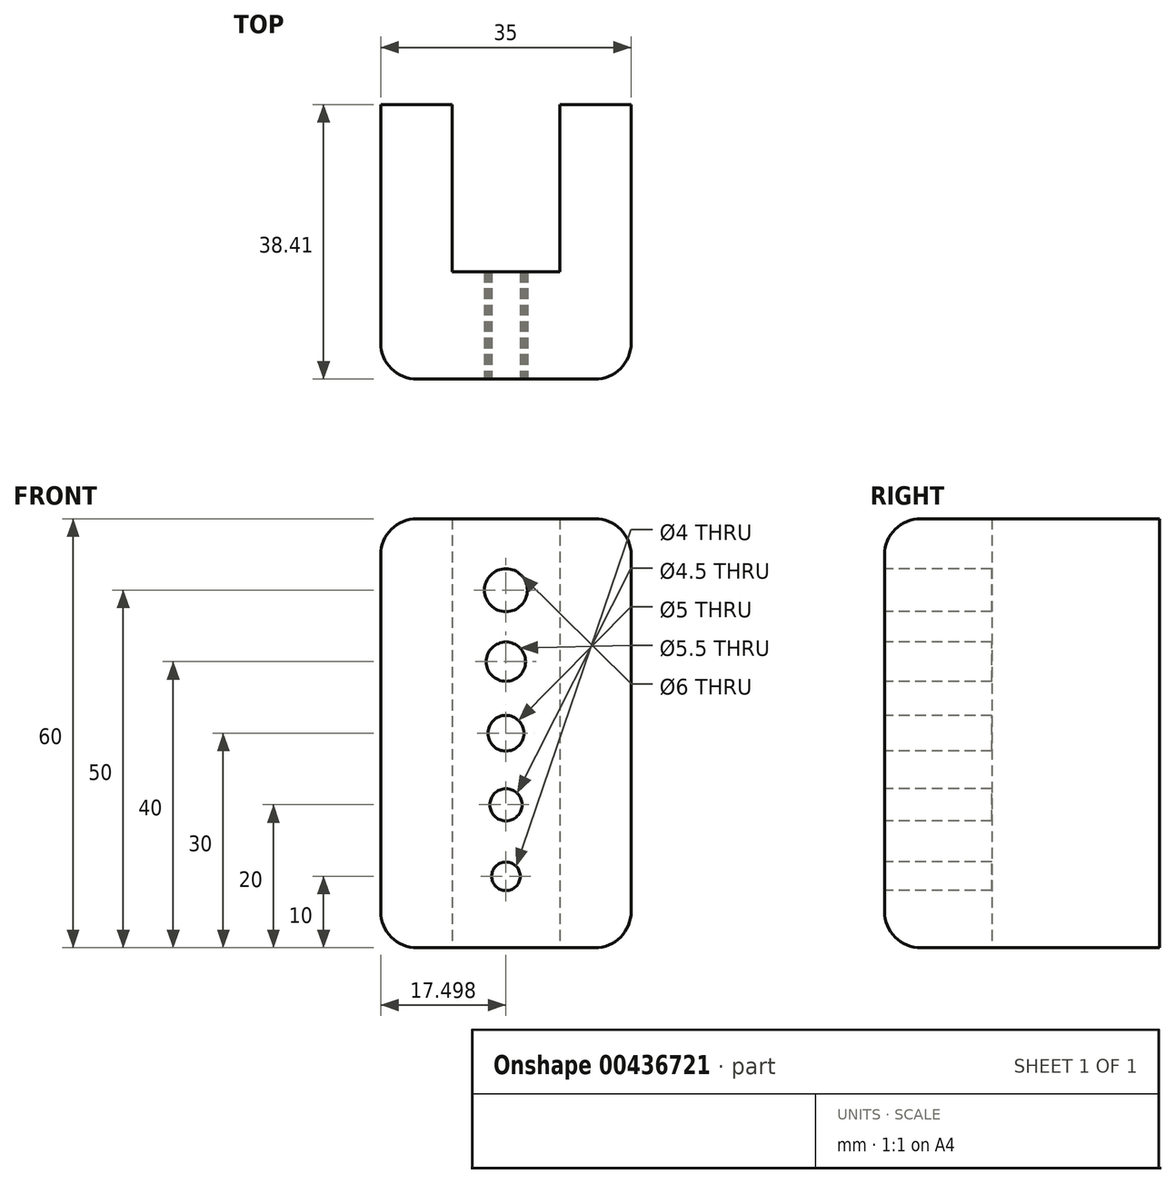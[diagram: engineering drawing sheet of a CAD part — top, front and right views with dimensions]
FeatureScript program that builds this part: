
annotation { "Feature Type Name" : "Feature", "Feature Type Description" : "" }
export const myFeature = defineFeature(function(context is Context, id is Id, definition is map)
    precondition{}
    {
        {
            var Q0;
            Q0=qCreatedBy(makeId("Top.planeOp"),FACE);
            var sketch = newSketch(context, id + "F0", { "sketchPlane" : qUnion([Q0])});
            skLineSegment(sketch, "E0", {"start": v(-17.33, 0) * mm, "end": v(16.64, 0) * mm});
            skLineSegment(sketch, "E1", {"start": v(16.64, 0) * mm, "end": v(16.64, 38.4) * mm});
            skLineSegment(sketch, "E2", {"start": v(16.64, 38.4) * mm, "end": v(6.64, 38.4) * mm});
            skLineSegment(sketch, "E3", {"start": v(6.64, 38.4) * mm, "end": v(6.64, 15) * mm});
            skLineSegment(sketch, "E4", {"start": v(6.64, 15) * mm, "end": v(-8.36, 15) * mm});
            skLineSegment(sketch, "E5", {"start": v(-8.36, 15) * mm, "end": v(-8.36, 38.4) * mm});
            skLineSegment(sketch, "E6", {"start": v(-8.36, 38.4) * mm, "end": v(-18.36, 38.4) * mm});
            skLineSegment(sketch, "E7", {"start": v(-18.36, 38.4) * mm, "end": v(-18.36, 0) * mm});
            skLineSegment(sketch, "E8", {"start": v(-17.33, 0) * mm, "end": v(-18.36, 0) * mm});
            skSolve(sketch);
        }
        {
            var Q0;
            Q0 = qSketchRegion(id + "F0", true);
            extrude(context, id + "F1", {"entities" : qUnion([Q0]), "depth" : 60 * mm});
        }
        {
            var Q0;
            Q0=makeQuery(id+"F1.opExtrude","SWEPT_FACE",FACE,{"disambiguationData":[OSD([sQuery(id+"F0.wireOp",EDGE,"E0"),sQuery(id+"F0.wireOp",EDGE,"E8")])]});
            var sketch = newSketch(context, id + "F2", { "sketchPlane" : qUnion([Q0])});
            skCircle(sketch, "E9", {"center": v(-0.86, 10) * mm, "radius": 2 * mm});
            skCircle(sketch, "E10", {"center": v(-0.86, 30) * mm, "radius": 2.5 * mm});
            skCircle(sketch, "E11", {"center": v(-0.86, 40) * mm, "radius": 2.75 * mm});
            skCircle(sketch, "E12", {"center": v(-0.86, 50) * mm, "radius": 3 * mm});
            skCircle(sketch, "E13", {"center": v(-0.86, 20) * mm, "radius": 2.25 * mm});
            skSolve(sketch);
        }
        {
            var Q0;
            Q0=sQuery(id+"F2.wireOp",VERTEX,"E9.center");
            var Q1;
            Q1=makeQuery(id+"F1.opExtrude","SWEPT_BODY",BODY,{"disambiguationData":[OSD([sQuery(id+"F0.wireOp",EDGE,"E0"),sQuery(id+"F0.wireOp",EDGE,"E1"),sQuery(id+"F0.wireOp",EDGE,"E2"),sQuery(id+"F0.wireOp",EDGE,"E3"),sQuery(id+"F0.wireOp",EDGE,"E4"),sQuery(id+"F0.wireOp",EDGE,"E5"),sQuery(id+"F0.wireOp",EDGE,"E6"),sQuery(id+"F0.wireOp",EDGE,"E7"),sQuery(id+"F0.wireOp",EDGE,"E8")])]});
            hole(context, id + "F3", {"style" : HoleStyle.SIMPLE, "endStyle" : HoleEndStyle.THROUGH, "holeDiameter" : 4 * mm, "isTappedThrough" : true, "tappedDepth" : 12.7 * mm, "tapClearance" : 3, "locations" : qUnion([Q0]), "scope" : qUnion([Q1])});
        }
        {
            var Q0;
            Q0=sQuery(id+"F2.wireOp",VERTEX,"E13.center");
            var Q1;
            Q1=makeQuery(id+"F1.opExtrude","SWEPT_BODY",BODY,{"disambiguationData":[OSD([sQuery(id+"F0.wireOp",EDGE,"E0"),sQuery(id+"F0.wireOp",EDGE,"E1"),sQuery(id+"F0.wireOp",EDGE,"E2"),sQuery(id+"F0.wireOp",EDGE,"E3"),sQuery(id+"F0.wireOp",EDGE,"E4"),sQuery(id+"F0.wireOp",EDGE,"E5"),sQuery(id+"F0.wireOp",EDGE,"E6"),sQuery(id+"F0.wireOp",EDGE,"E7"),sQuery(id+"F0.wireOp",EDGE,"E8")])]});
            hole(context, id + "F4", {"style" : HoleStyle.SIMPLE, "endStyle" : HoleEndStyle.THROUGH, "holeDiameter" : 4.5 * mm, "isTappedThrough" : true, "tappedDepth" : 12.7 * mm, "tapClearance" : 3, "locations" : qUnion([Q0]), "scope" : qUnion([Q1])});
        }
        {
            var Q0;
            Q0=sQuery(id+"F2.wireOp",VERTEX,"E10.center");
            var Q1;
            Q1=makeQuery(id+"F1.opExtrude","SWEPT_BODY",BODY,{"disambiguationData":[OSD([sQuery(id+"F0.wireOp",EDGE,"E0"),sQuery(id+"F0.wireOp",EDGE,"E1"),sQuery(id+"F0.wireOp",EDGE,"E2"),sQuery(id+"F0.wireOp",EDGE,"E3"),sQuery(id+"F0.wireOp",EDGE,"E4"),sQuery(id+"F0.wireOp",EDGE,"E5"),sQuery(id+"F0.wireOp",EDGE,"E6"),sQuery(id+"F0.wireOp",EDGE,"E7"),sQuery(id+"F0.wireOp",EDGE,"E8")])]});
            hole(context, id + "F5", {"style" : HoleStyle.SIMPLE, "endStyle" : HoleEndStyle.THROUGH, "holeDiameter" : 5 * mm, "isTappedThrough" : true, "tappedDepth" : 12.7 * mm, "tapClearance" : 3, "locations" : qUnion([Q0]), "scope" : qUnion([Q1])});
        }
        {
            var Q0;
            Q0=sQuery(id+"F2.wireOp",VERTEX,"E11.center");
            var Q1;
            Q1=makeQuery(id+"F1.opExtrude","SWEPT_BODY",BODY,{"disambiguationData":[OSD([sQuery(id+"F0.wireOp",EDGE,"E0"),sQuery(id+"F0.wireOp",EDGE,"E1"),sQuery(id+"F0.wireOp",EDGE,"E2"),sQuery(id+"F0.wireOp",EDGE,"E3"),sQuery(id+"F0.wireOp",EDGE,"E4"),sQuery(id+"F0.wireOp",EDGE,"E5"),sQuery(id+"F0.wireOp",EDGE,"E6"),sQuery(id+"F0.wireOp",EDGE,"E7"),sQuery(id+"F0.wireOp",EDGE,"E8")])]});
            hole(context, id + "F6", {"style" : HoleStyle.SIMPLE, "endStyle" : HoleEndStyle.THROUGH, "holeDiameter" : 5.5 * mm, "isTappedThrough" : true, "tappedDepth" : 12.7 * mm, "tapClearance" : 3, "locations" : qUnion([Q0]), "scope" : qUnion([Q1])});
        }
        {
            var Q0;
            Q0=sQuery(id+"F2.wireOp",VERTEX,"E12.center");
            var Q1;
            Q1=makeQuery(id+"F1.opExtrude","SWEPT_BODY",BODY,{"disambiguationData":[OSD([sQuery(id+"F0.wireOp",EDGE,"E0"),sQuery(id+"F0.wireOp",EDGE,"E1"),sQuery(id+"F0.wireOp",EDGE,"E2"),sQuery(id+"F0.wireOp",EDGE,"E3"),sQuery(id+"F0.wireOp",EDGE,"E4"),sQuery(id+"F0.wireOp",EDGE,"E5"),sQuery(id+"F0.wireOp",EDGE,"E6"),sQuery(id+"F0.wireOp",EDGE,"E7"),sQuery(id+"F0.wireOp",EDGE,"E8")])]});
            hole(context, id + "F7", {"style" : HoleStyle.SIMPLE, "endStyle" : HoleEndStyle.THROUGH, "holeDiameter" : 6 * mm, "isTappedThrough" : true, "tappedDepth" : 12.7 * mm, "tapClearance" : 3, "locations" : qUnion([Q0]), "scope" : qUnion([Q1])});
        }
        {
            var Q0;
            Q0=makeQuery(id+"F1.opExtrude","SWEPT_EDGE",EDGE,{"disambiguationData":[OSD([sQuery(id+"F0.wireOp",EDGE,"E0"),sQuery(id+"F0.wireOp",EDGE,"E1")])]});
            var Q1;
            Q1=makeQuery(id+"F1.opExtrude","CAP_EDGE",EDGE,{"disambiguationData":[OSD([sQuery(id+"F0.wireOp",EDGE,"E0"),sQuery(id+"F0.wireOp",EDGE,"E8")])],"isStart":false});
            var Q2;
            Q2=makeQuery(id+"F1.opExtrude","SWEPT_EDGE",EDGE,{"disambiguationData":[OSD([sQuery(id+"F0.wireOp",EDGE,"E7"),sQuery(id+"F0.wireOp",EDGE,"E8")])]});
            var Q3;
            Q3=makeQuery(id+"F1.opExtrude","CAP_EDGE",EDGE,{"disambiguationData":[OSD([sQuery(id+"F0.wireOp",EDGE,"E0"),sQuery(id+"F0.wireOp",EDGE,"E8")])],"isStart":true});
            var Q4;
            Q4=makeQuery(id+"F1.opExtrude","CAP_EDGE",EDGE,{"disambiguationData":[OSD([sQuery(id+"F0.wireOp",EDGE,"E7")])],"isStart":false});
            var Q5;
            Q5=makeQuery(id+"F1.opExtrude","CAP_EDGE",EDGE,{"disambiguationData":[OSD([sQuery(id+"F0.wireOp",EDGE,"E1")])],"isStart":false});
            var Q6;
            Q6=makeQuery(id+"F1.opExtrude","CAP_EDGE",EDGE,{"disambiguationData":[OSD([sQuery(id+"F0.wireOp",EDGE,"E7")])],"isStart":true});
            var Q7;
            Q7=makeQuery(id+"F1.opExtrude","CAP_EDGE",EDGE,{"disambiguationData":[OSD([sQuery(id+"F0.wireOp",EDGE,"E1")])],"isStart":true});
            fillet(context, id + "F8", {"entities" : qUnion([Q0, Q1, Q2, Q3, Q4, Q5, Q6, Q7]), "radius" : 5.08 * mm, "tangentPropagation" : true, "allowEdgeOverflow" : false});
        }
    });
